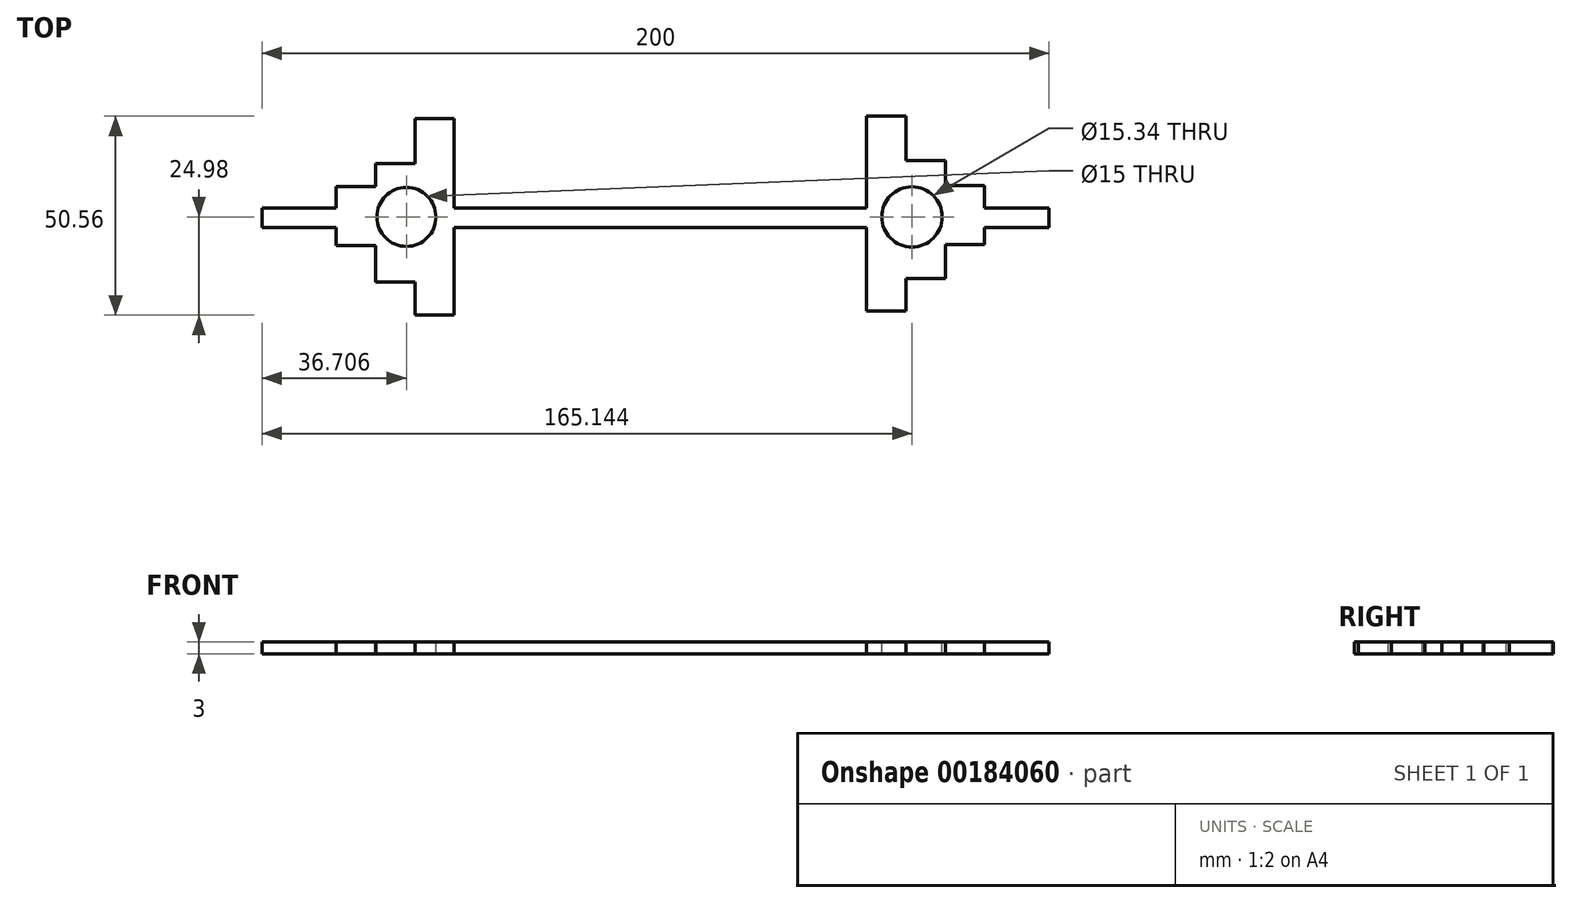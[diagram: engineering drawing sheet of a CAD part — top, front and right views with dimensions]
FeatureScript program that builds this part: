
annotation { "Feature Type Name" : "Feature", "Feature Type Description" : "" }
export const myFeature = defineFeature(function(context is Context, id is Id, definition is map)
    precondition{}
    {
        {
            var Q0;
            Q0=qCreatedBy(makeId("Top.planeOp"),FACE);
            var sketch = newSketch(context, id + "F0", { "sketchPlane" : qUnion([Q0])});
            skLineSegment(sketch, "E0.bottom", {"start": v(-99.58, 2.27) * mm, "end": v(-80.71, 2.27) * mm});
            skLineSegment(sketch, "E0.top", {"start": v(-99.58, -2.73) * mm, "end": v(-80.71, -2.73) * mm});
            skLineSegment(sketch, "E0.left", {"start": v(-99.58, 2.27) * mm, "end": v(-99.58, -2.73) * mm});
            skLineSegment(sketch, "E0.right", {"start": v(100.42, 2.27) * mm, "end": v(100.42, -2.73) * mm});
            skLineSegment(sketch, "E1.bottom", {"start": v(-60.71, 25.02) * mm, "end": v(-50.71, 25.02) * mm});
            skLineSegment(sketch, "E1.top", {"start": v(-60.71, -24.98) * mm, "end": v(-50.71, -24.98) * mm});
            skLineSegment(sketch, "E1.left", {"start": v(-60.71, 25.02) * mm, "end": v(-60.71, 13.5) * mm});
            skLineSegment(sketch, "E1.right", {"start": v(-50.71, 25.02) * mm, "end": v(-50.71, 2.27) * mm});
            skLineSegment(sketch, "E2.bottom", {"start": v(-70.71, 13.5) * mm, "end": v(-60.71, 13.5) * mm});
            skLineSegment(sketch, "E2.top", {"start": v(-70.71, -16.5) * mm, "end": v(-60.71, -16.5) * mm});
            skLineSegment(sketch, "E2.left", {"start": v(-70.71, 13.5) * mm, "end": v(-70.71, 7.67) * mm});
            skLineSegment(sketch, "E3.bottom", {"start": v(-80.71, 7.67) * mm, "end": v(-70.71, 7.67) * mm});
            skLineSegment(sketch, "E3.top", {"start": v(-80.71, -7.33) * mm, "end": v(-70.71, -7.33) * mm});
            skLineSegment(sketch, "E3.left", {"start": v(-80.71, 7.67) * mm, "end": v(-80.71, 2.27) * mm});
            skLineSegment(sketch, "E4.bottom", {"start": v(64.03, -23.96) * mm, "end": v(54.03, -23.96) * mm});
            skLineSegment(sketch, "E4.top", {"start": v(64.03, 25.58) * mm, "end": v(54.03, 25.58) * mm});
            skLineSegment(sketch, "E4.left", {"start": v(64.03, -23.96) * mm, "end": v(64.03, -15.64) * mm});
            skLineSegment(sketch, "E4.right", {"start": v(54.03, -23.96) * mm, "end": v(54.03, -2.73) * mm});
            skLineSegment(sketch, "E5.bottom", {"start": v(74.03, -15.64) * mm, "end": v(64.03, -15.64) * mm});
            skLineSegment(sketch, "E5.top", {"start": v(74.03, 14.36) * mm, "end": v(64.03, 14.36) * mm});
            skLineSegment(sketch, "E5.left", {"start": v(74.03, -15.64) * mm, "end": v(74.03, -7.07) * mm});
            skLineSegment(sketch, "E6.bottom", {"start": v(84.03, -7.07) * mm, "end": v(74.03, -7.07) * mm});
            skLineSegment(sketch, "E6.top", {"start": v(84.03, 7.93) * mm, "end": v(74.03, 7.93) * mm});
            skLineSegment(sketch, "E6.left", {"start": v(84.03, -7.07) * mm, "end": v(84.03, -2.73) * mm});
            skLineSegment(sketch, "E7.trimOffspring", {"start": v(-50.71, -2.73) * mm, "end": v(54.03, -2.73) * mm});
            skLineSegment(sketch, "E8.trimOffspring", {"start": v(-50.71, 2.27) * mm, "end": v(54.03, 2.27) * mm});
            skLineSegment(sketch, "E9.trimOffspring", {"start": v(-70.71, -7.33) * mm, "end": v(-70.71, -16.5) * mm});
            skLineSegment(sketch, "E10.trimOffspring", {"start": v(-60.71, -16.5) * mm, "end": v(-60.71, -24.98) * mm});
            skLineSegment(sketch, "E11.trimOffspring", {"start": v(-80.71, -2.73) * mm, "end": v(-80.71, -7.33) * mm});
            skLineSegment(sketch, "E12.trimOffspring", {"start": v(84.03, 2.27) * mm, "end": v(100.42, 2.27) * mm});
            skLineSegment(sketch, "E13.trimOffspring", {"start": v(84.03, -2.73) * mm, "end": v(100.42, -2.73) * mm});
            skLineSegment(sketch, "E14.trimOffspring", {"start": v(64.03, 14.36) * mm, "end": v(64.03, 25.58) * mm});
            skLineSegment(sketch, "E15.trimOffspring", {"start": v(74.03, 7.93) * mm, "end": v(74.03, 14.36) * mm});
            skLineSegment(sketch, "E16.trimOffspring", {"start": v(84.03, 2.27) * mm, "end": v(84.03, 7.93) * mm});
            skLineSegment(sketch, "E17.trimOffspring", {"start": v(54.03, 2.27) * mm, "end": v(54.03, 25.58) * mm});
            skLineSegment(sketch, "E18.trimOffspring", {"start": v(-50.71, -2.73) * mm, "end": v(-50.71, -24.98) * mm});
            skSolve(sketch);
        }
        {
            var Q0;
            Q0 = qSketchRegion(id + "F0", true);
            extrude(context, id + "F1", {"entities" : qUnion([Q0]), "depth" : 3 * mm});
        }
        {
            var Q0;
            Q0=makeQuery(id+"F1.opExtrude","CAP_FACE",FACE,{"disambiguationData":[OSD([sQuery(id+"F0.wireOp",EDGE,"E0.bottom"),sQuery(id+"F0.wireOp",EDGE,"E0.top"),sQuery(id+"F0.wireOp",EDGE,"E0.left"),sQuery(id+"F0.wireOp",EDGE,"E0.right"),sQuery(id+"F0.wireOp",EDGE,"E1.bottom"),sQuery(id+"F0.wireOp",EDGE,"E1.top"),sQuery(id+"F0.wireOp",EDGE,"E1.left"),sQuery(id+"F0.wireOp",EDGE,"E1.right"),sQuery(id+"F0.wireOp",EDGE,"E2.bottom"),sQuery(id+"F0.wireOp",EDGE,"E2.top"),sQuery(id+"F0.wireOp",EDGE,"E2.left"),sQuery(id+"F0.wireOp",EDGE,"E3.bottom"),sQuery(id+"F0.wireOp",EDGE,"E3.top"),sQuery(id+"F0.wireOp",EDGE,"E3.left"),sQuery(id+"F0.wireOp",EDGE,"E4.bottom"),sQuery(id+"F0.wireOp",EDGE,"E4.top"),sQuery(id+"F0.wireOp",EDGE,"E4.left"),sQuery(id+"F0.wireOp",EDGE,"E4.right"),sQuery(id+"F0.wireOp",EDGE,"E5.bottom"),sQuery(id+"F0.wireOp",EDGE,"E5.top"),sQuery(id+"F0.wireOp",EDGE,"E5.left"),sQuery(id+"F0.wireOp",EDGE,"E6.bottom"),sQuery(id+"F0.wireOp",EDGE,"E6.top"),sQuery(id+"F0.wireOp",EDGE,"E6.left"),sQuery(id+"F0.wireOp",EDGE,"E7.trimOffspring"),sQuery(id+"F0.wireOp",EDGE,"E8.trimOffspring"),sQuery(id+"F0.wireOp",EDGE,"E9.trimOffspring"),sQuery(id+"F0.wireOp",EDGE,"E10.trimOffspring"),sQuery(id+"F0.wireOp",EDGE,"E11.trimOffspring"),sQuery(id+"F0.wireOp",EDGE,"E12.trimOffspring"),sQuery(id+"F0.wireOp",EDGE,"E13.trimOffspring"),sQuery(id+"F0.wireOp",EDGE,"E14.trimOffspring"),sQuery(id+"F0.wireOp",EDGE,"E15.trimOffspring"),sQuery(id+"F0.wireOp",EDGE,"E16.trimOffspring"),sQuery(id+"F0.wireOp",EDGE,"E17.trimOffspring"),sQuery(id+"F0.wireOp",EDGE,"E18.trimOffspring")])],"isStart":false});
            var sketch = newSketch(context, id + "F2", { "sketchPlane" : qUnion([Q0])});
            skCircle(sketch, "E19", {"center": v(-62.87, 0) * mm, "radius": 7.5 * mm});
            skCircle(sketch, "E20", {"center": v(65.56, 0) * mm, "radius": 7.67 * mm});
            skSolve(sketch);
        }
        {
            var Q0;
            Q0 = qSketchRegion(id + "F2", true);
            extrude(context, id + "F3", {"entities" : qUnion([Q0]), "operationType" : NewBodyOperationType.REMOVE, "endBound" : BoundingType.UP_TO_NEXT, "oppositeDirection" : true, "depth" : 25 * mm});
        }
    });
